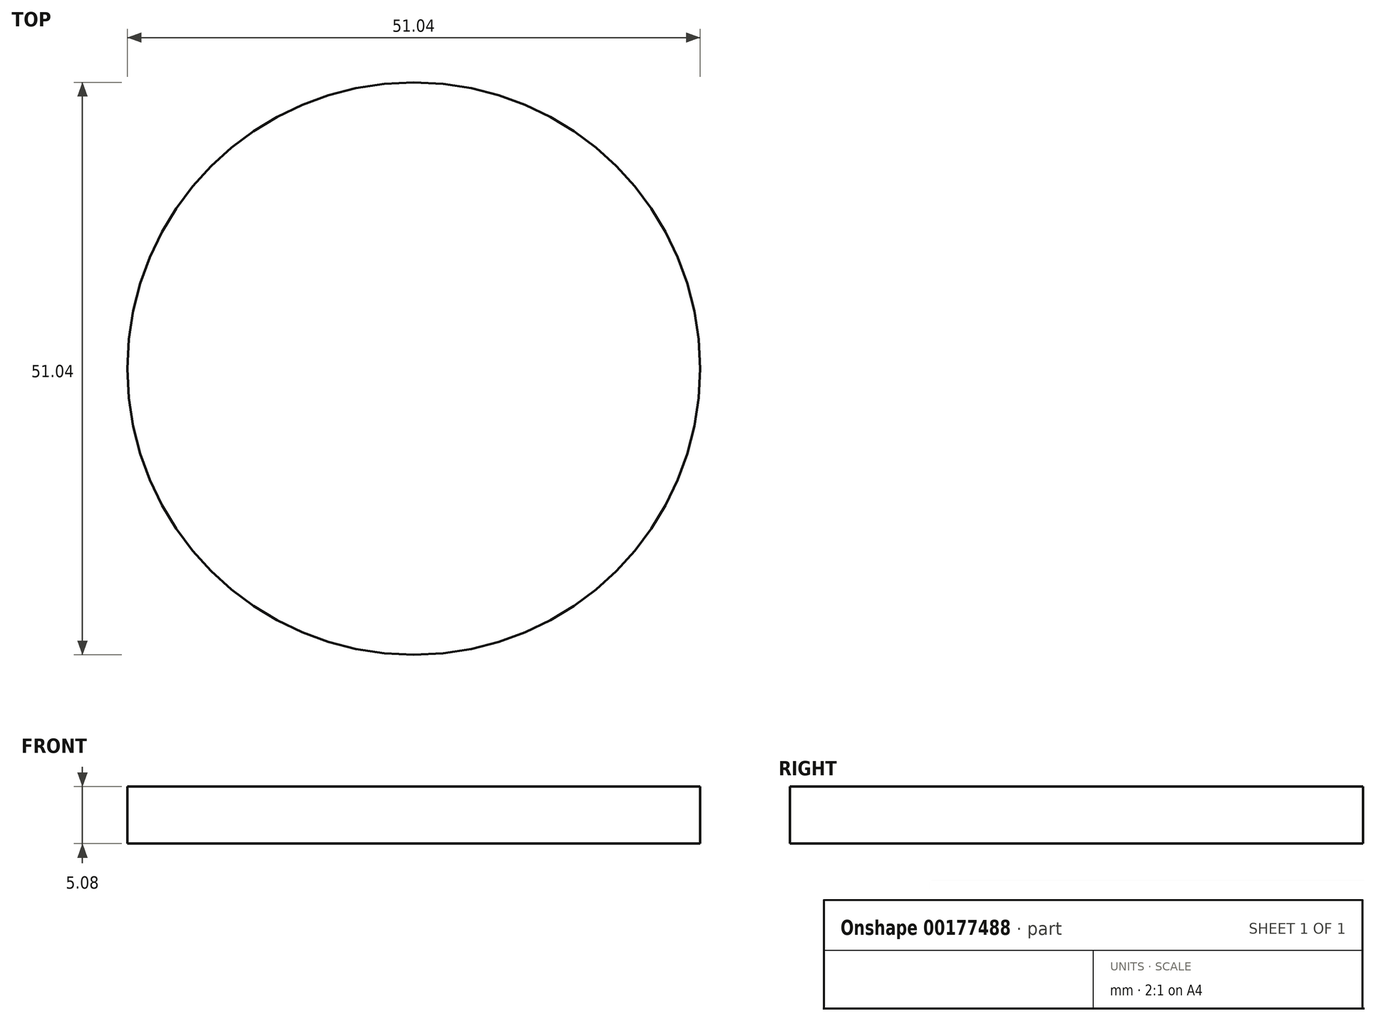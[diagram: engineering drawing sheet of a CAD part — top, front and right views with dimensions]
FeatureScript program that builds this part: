
annotation { "Feature Type Name" : "Feature", "Feature Type Description" : "" }
export const myFeature = defineFeature(function(context is Context, id is Id, definition is map)
    precondition{}
    {
        {
            var Q0;
            Q0=qCreatedBy(makeId("Top.planeOp"),FACE);
            var sketch = newSketch(context, id + "F0", { "sketchPlane" : qUnion([Q0])});
            skCircle(sketch, "E0", {"center": v(0, 0) * mm, "radius": 25.52 * mm});
            skSolve(sketch);
        }
        {
            var Q0;
            Q0=makeQuery(id+"F0.imprint","IMPRINT",FACE,{"disambiguationData":[TD([[makeQuery(id+"F0.imprint","IMPRINT",EDGE,{"derivedFrom":sQuery(id+"F0.wireOp",EDGE,"E0")}),1.0]])]});
            extrude(context, id + "F1", {"entities" : qUnion([Q0]), "depth" : 5.08 * mm});
        }
    });
